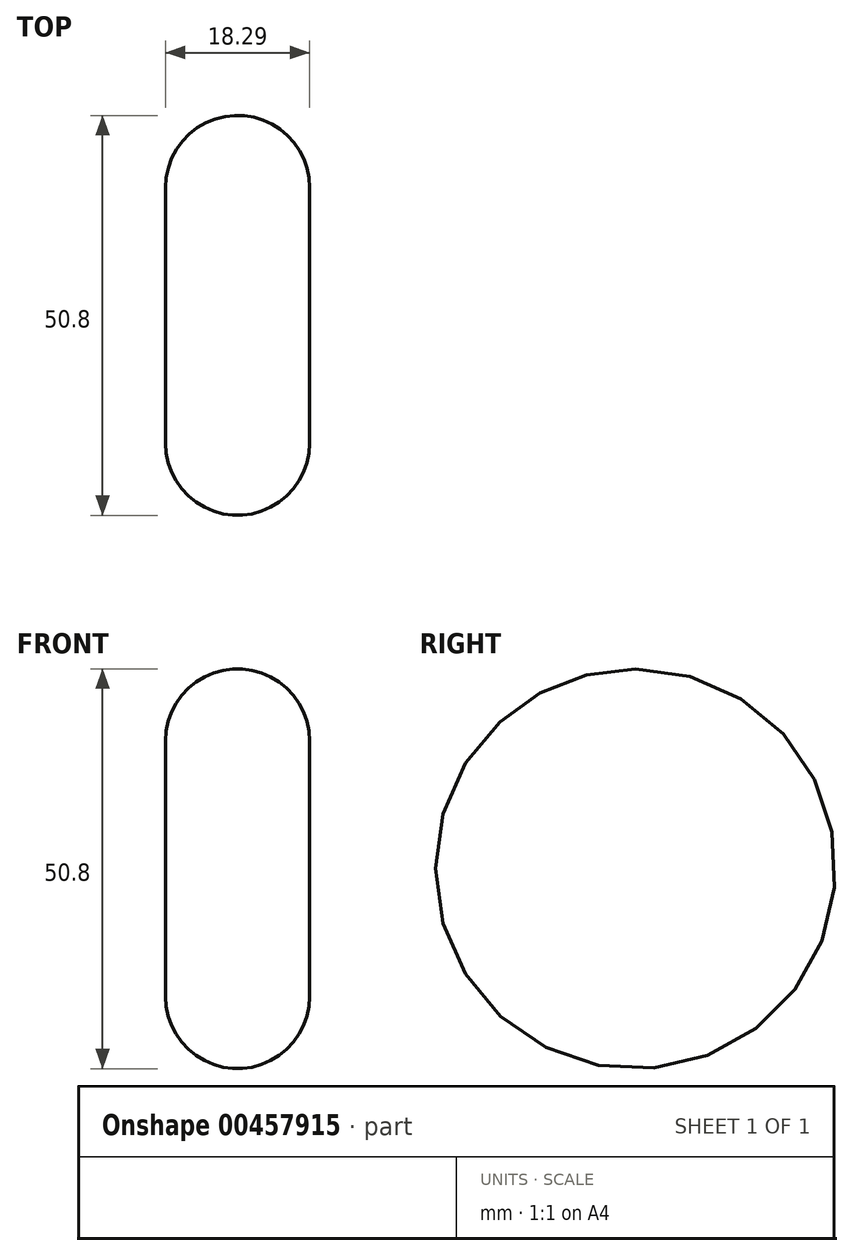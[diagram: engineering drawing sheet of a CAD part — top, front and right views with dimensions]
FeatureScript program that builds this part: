
annotation { "Feature Type Name" : "Feature", "Feature Type Description" : "" }
export const myFeature = defineFeature(function(context is Context, id is Id, definition is map)
    precondition{}
    {
        {
            var Q0;
            Q0=qCreatedBy(makeId("Front.planeOp"),FACE);
            var sketch = newSketch(context, id + "F0", { "sketchPlane" : qUnion([Q0])});
            skLineSegment(sketch, "E0.bottom", {"start": v(-30.76, 33.01) * mm, "end": v(-12.47, 33.01) * mm});
            skLineSegment(sketch, "E0.left", {"start": v(-30.76, 33.01) * mm, "end": v(-30.76, 49.27) * mm});
            skLineSegment(sketch, "E0.right", {"start": v(-12.47, 33.01) * mm, "end": v(-12.47, 49.27) * mm});
            skArc(sketch, "E1", {"start": v(-30.76, 49.27) * mm, "mid": v(-21.61, 58.41) * mm, "end": v(-12.47, 49.27) * mm});
            skLineSegment(sketch, "E2", {"start": v(-21.61, 58.41) * mm, "end": v(-21.61, 33.01) * mm, "construction": true});
            skSolve(sketch);
        }
        {
            var Q0;
            Q0=makeQuery(id+"F0.imprint","IMPRINT",FACE,{"disambiguationData":[TD([[makeQuery(id+"F0.imprint","IMPRINT",EDGE,{"derivedFrom":sQuery(id+"F0.wireOp",EDGE,"E0.bottom")}),1.0]])]});
            var Q1;
            Q1=sQuery(id+"F0.wireOp",EDGE,"E0.bottom");
            revolve(context, id + "F1", {"entities" : qUnion([Q0]), "axis" : qUnion([Q1]), "revolveType" : RevolveType.FULL});
        }
    });
